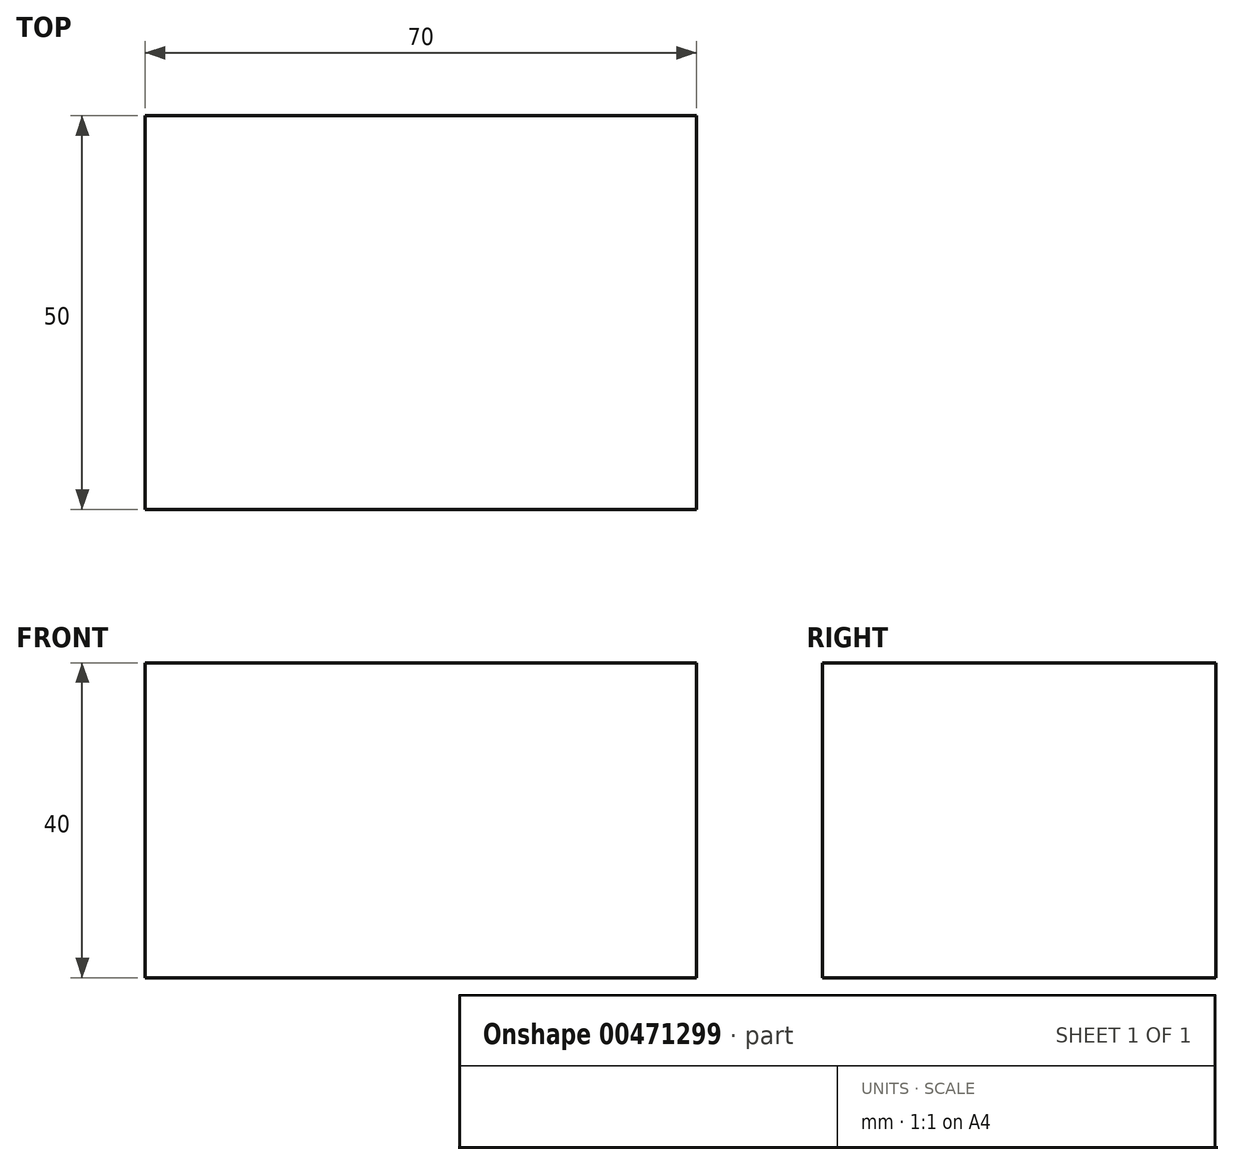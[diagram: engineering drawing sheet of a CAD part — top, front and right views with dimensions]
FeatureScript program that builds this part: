
annotation { "Feature Type Name" : "Feature", "Feature Type Description" : "" }
export const myFeature = defineFeature(function(context is Context, id is Id, definition is map)
    precondition{}
    {
        {
            var Q0;
            Q0=qCreatedBy(makeId("Front.planeOp"),FACE);
            var sketch = newSketch(context, id + "F0", { "sketchPlane" : qUnion([Q0])});
            skLineSegment(sketch, "E0.bottom", {"start": v(40, 25) * mm, "end": v(-40, 25) * mm});
            skLineSegment(sketch, "E0.top", {"start": v(40, -25) * mm, "end": v(-40, -25) * mm});
            skLineSegment(sketch, "E0.left", {"start": v(40, 25) * mm, "end": v(40, -25) * mm});
            skLineSegment(sketch, "E0.right", {"start": v(-40, 25) * mm, "end": v(-40, -25) * mm});
            skPoint(sketch, "E0.middle", {"position": v(0, 0) * mm});
            skLineSegment(sketch, "E1.bottom", {"start": v(-38.55, 20) * mm, "end": v(31.45, 20) * mm});
            skLineSegment(sketch, "E1.top", {"start": v(-38.55, -20) * mm, "end": v(31.45, -20) * mm});
            skLineSegment(sketch, "E1.left", {"start": v(-38.55, 20) * mm, "end": v(-38.55, -20) * mm});
            skLineSegment(sketch, "E1.right", {"start": v(31.45, 20) * mm, "end": v(31.45, -20) * mm});
            skPoint(sketch, "E1.middle", {"position": v(-3.55, 0) * mm});
            skSolve(sketch);
        }
        {
            var Q0;
            Q0=makeQuery(id+"F0.imprint","IMPRINT",FACE,{"disambiguationData":[TD([[makeQuery(id+"F0.imprint","IMPRINT",EDGE,{"derivedFrom":sQuery(id+"F0.wireOp",EDGE,"E1.bottom")}),-1.0]])]});
            extrude(context, id + "F1", {"entities" : qUnion([Q0]), "depth" : 25 * mm});
        }
        {
            var Q0;
            Q0=makeQuery(id+"F1.opExtrude","CAP_FACE",FACE,{"disambiguationData":[OSD([sQuery(id+"F0.wireOp",EDGE,"E1.bottom"),sQuery(id+"F0.wireOp",EDGE,"E1.top"),sQuery(id+"F0.wireOp",EDGE,"E1.left"),sQuery(id+"F0.wireOp",EDGE,"E1.right")])],"isStart":true});
            extrude(context, id + "F2", {"entities" : qUnion([Q0]), "operationType" : NewBodyOperationType.ADD, "depth" : 25 * mm});
        }
    });
